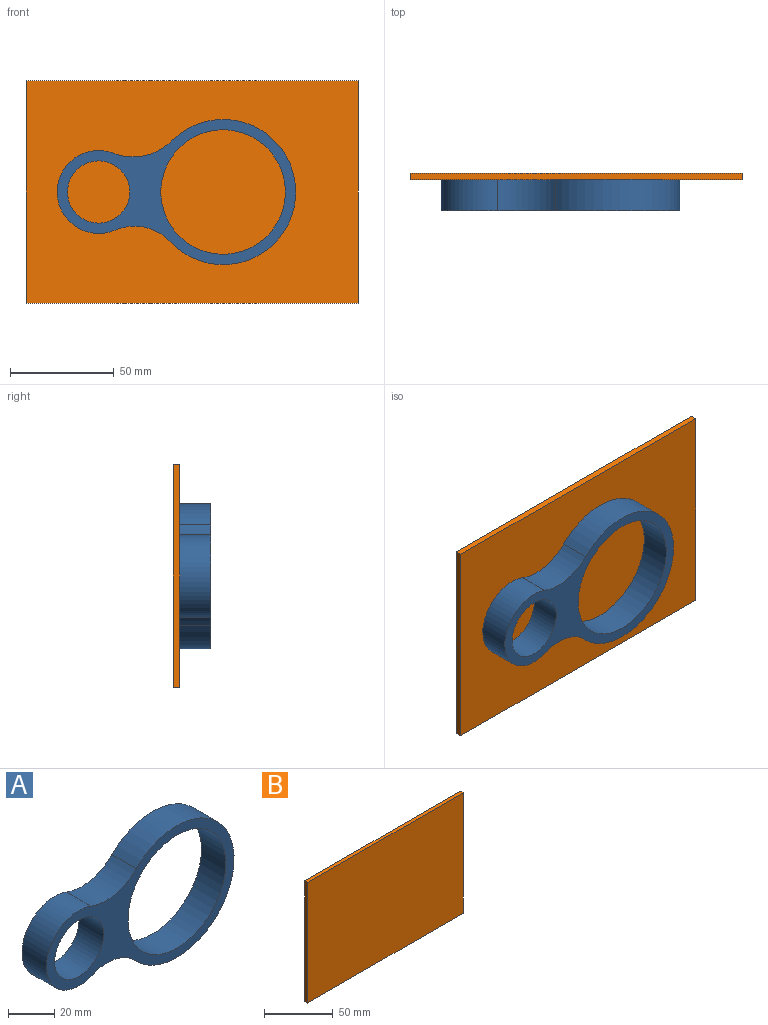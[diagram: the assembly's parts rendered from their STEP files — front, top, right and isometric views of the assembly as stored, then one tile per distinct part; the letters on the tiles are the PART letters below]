
ASSEMBLY  parts=2 mates=1
PART A: 8 faces, bbox 115x15x70 mm
  f0: cylinder r=20mm len=40mm, axis (0,1,0), area 1175.9mm2, adj f1,f3,f6,f7
  f1: cylinder r=23.53mm len=26.51mm, axis (0,1,0), area 432.9mm2, adj f0,f2,f6,f7
  f2: cylinder r=35mm len=70mm, axis (0,1,0), area 2495mm2, adj f1,f3,f6,f7
  f3: cylinder r=25.93mm len=27.85mm, axis (0,1,0), area 452.2mm2, adj f0,f2,f6,f7
  f4: cylinder r=15mm len=30mm, axis (0,1,0), area 1413.7mm2, adj f6,f7
  f5: cylinder r=30mm len=60mm, axis (0,1,0), area 2827.4mm2, adj f6,f7
  f6: plane 115x70mm, normal (0,-1,0), area 1913.6mm2, adj f0,f1,f2,f3,f4,f5
  f7: plane 115x70mm, normal (0,1,0), area 1913.6mm2, adj f0,f1,f2,f3,f4,f5
PART B: 6 faces, bbox 160x3x107 mm
  f0: plane 107.04x3mm, normal (-1,0,0), area 321.1mm2, adj f1,f3,f4,f5
  f1: plane 160x3mm, normal (0,0,-1), area 480mm2, adj f0,f2,f4,f5
  f2: plane 107.04x3mm, normal (1,0,0), area 321.1mm2, adj f1,f3,f4,f5
  f3: plane 160x3mm, normal (0,0,1), area 480mm2, adj f0,f2,f4,f5
  f4: plane 160x107.04mm, normal (0,-1,0), area 17126.8mm2, adj f0,f1,f2,f3
  f5: plane 160x107.04mm, normal (0,1,0), area 17126.8mm2, adj f0,f1,f2,f3
PLACE A t=(-116.23,-21.17,30.84)mm
PLACE B t=(-91.01,-18.17,33.8)mm
MATE fastened A.f2 <-> B.f4  axis (0,1,0) through (-87.33,-21.17,30.84)mm
